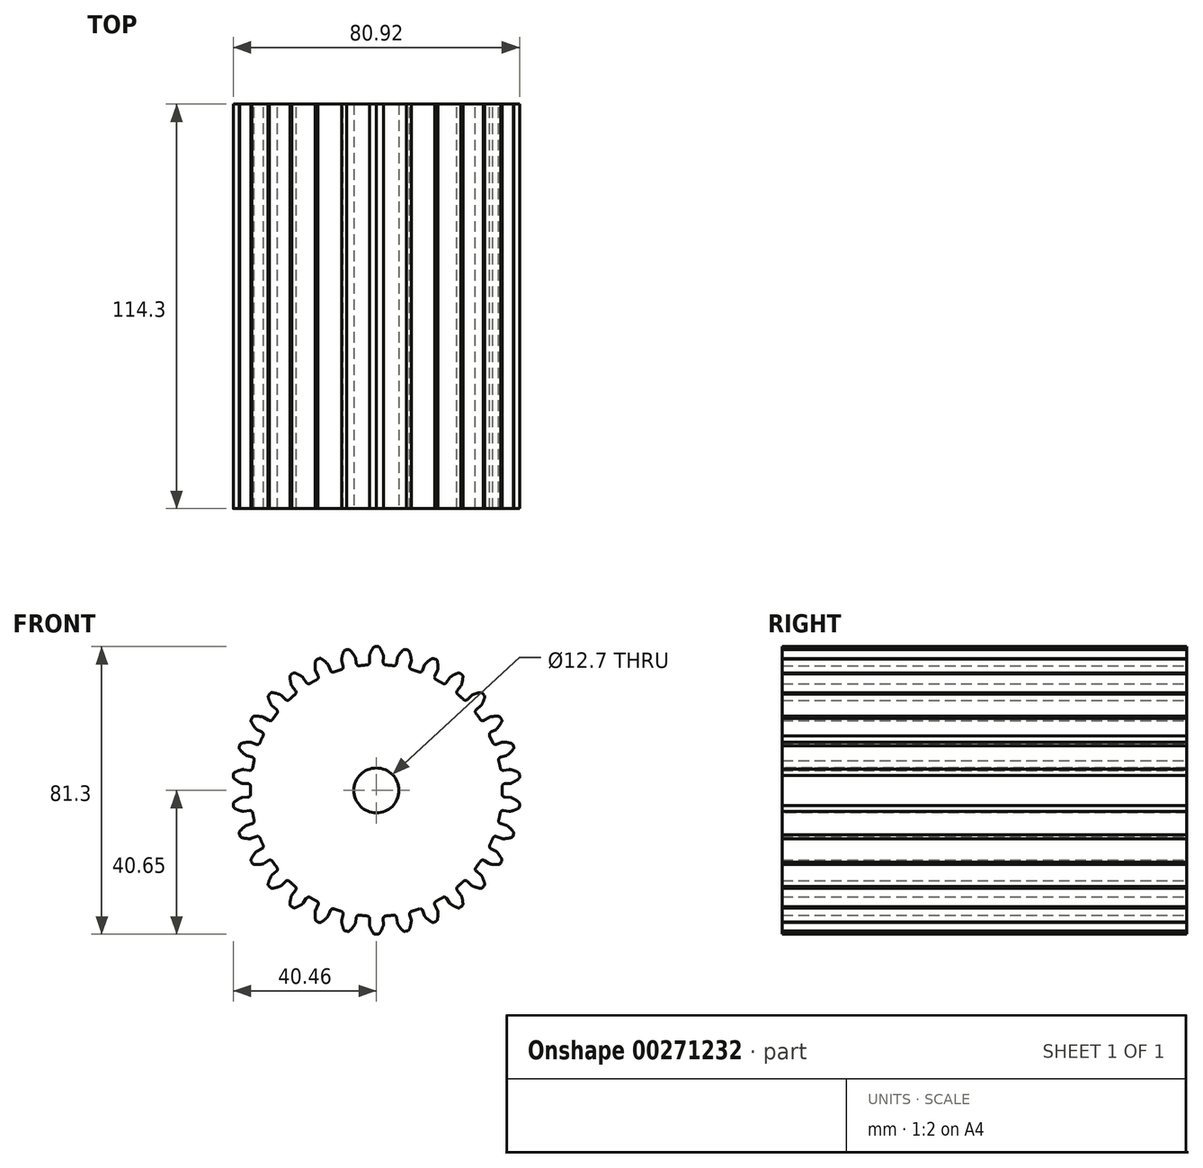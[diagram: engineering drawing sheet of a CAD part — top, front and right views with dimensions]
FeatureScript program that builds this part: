
annotation { "Feature Type Name" : "Feature", "Feature Type Description" : "" }
export const myFeature = defineFeature(function(context is Context, id is Id, definition is map)
    precondition{}
    {
        {
            var Q0;
            Q0=qCreatedBy(makeId("Front.planeOp"),FACE);
            var sketch = newSketch(context, id + "F0", { "sketchPlane" : qUnion([Q0])});
            skArc(sketch, "E0", {"start": v(-2.64, 35.46) * mm, "mid": v(-3.72, 35.37) * mm, "end": v(-4.8, 35.24) * mm});
            skArc(sketch, "E1.trimOffspring", {"start": v(1.94, 38.2) * mm, "mid": v(1.46, 39.34) * mm, "end": v(0.84, 40.41) * mm});
            skLineSegment(sketch, "E2", {"start": v(1.99, 37.9) * mm, "end": v(1.9, 36.3) * mm});
            skLineSegment(sketch, "E3", {"start": v(0.43, 40.64) * mm, "end": v(0, 40.65) * mm});
            skArc(sketch, "E4.MirrorCS", {"start": v(-1.94, 38.2) * mm, "mid": v(-1.5, 39.27) * mm, "end": v(-0.93, 40.28) * mm});
            skLineSegment(sketch, "E5.MirrorCS", {"start": v(-1.99, 37.9) * mm, "end": v(-1.9, 36.3) * mm});
            skLineSegment(sketch, "E6.MirrorCS", {"start": v(-0.28, 40.64) * mm, "end": v(0, 40.65) * mm});
            skPoint(sketch, "E7.visualSharp", {"position": v(-1.86, 35.51) * mm});
            skArc(sketch, "E7.filletArc", {"start": v(-2.64, 35.46) * mm, "mid": v(-2.1, 35.73) * mm, "end": v(-1.9, 36.3) * mm});
            skPoint(sketch, "E8.visualSharp", {"position": v(1.86, 35.51) * mm});
            skArc(sketch, "E8.filletArc", {"start": v(1.9, 36.3) * mm, "mid": v(2.1, 35.73) * mm, "end": v(2.64, 35.46) * mm});
            skPoint(sketch, "E9.visualSharp", {"position": v(2, 38.05) * mm});
            skArc(sketch, "E9.filletArc", {"start": v(1.99, 37.9) * mm, "mid": v(1.98, 38.05) * mm, "end": v(1.94, 38.2) * mm});
            skPoint(sketch, "E10.visualSharp", {"position": v(-2, 38.05) * mm});
            skArc(sketch, "E10.filletArc", {"start": v(-1.94, 38.2) * mm, "mid": v(-1.98, 38.05) * mm, "end": v(-1.99, 37.9) * mm});
            skPoint(sketch, "E11.visualSharp", {"position": v(0.69, 40.63) * mm});
            skArc(sketch, "E11.filletArc", {"start": v(0.84, 40.41) * mm, "mid": v(0.66, 40.58) * mm, "end": v(0.43, 40.64) * mm});
            skPoint(sketch, "E12.visualSharp", {"position": v(-0.69, 40.63) * mm});
            skArc(sketch, "E12.filletArc", {"start": v(-0.28, 40.64) * mm, "mid": v(-0.65, 40.54) * mm, "end": v(-0.93, 40.28) * mm});
            skLineSegment(sketch, "E13.1.0", {"start": v(-9.82, 36.66) * mm, "end": v(-9.4, 35.1) * mm});
            skArc(sketch, "E13.1.1", {"start": v(-9.95, 34.14) * mm, "mid": v(-9.48, 34.51) * mm, "end": v(-9.4, 35.1) * mm});
            skArc(sketch, "E13.1.2", {"start": v(-9.84, 36.96) * mm, "mid": v(-9.63, 38.1) * mm, "end": v(-9.28, 39.2) * mm});
            skArc(sketch, "E13.1.3", {"start": v(-6.04, 37.77) * mm, "mid": v(-6.75, 38.79) * mm, "end": v(-7.58, 39.7) * mm});
            skLineSegment(sketch, "E13.1.4", {"start": v(-5.94, 37.48) * mm, "end": v(-5.69, 35.9) * mm});
            skArc(sketch, "E13.1.5", {"start": v(-5.69, 35.9) * mm, "mid": v(-5.38, 35.38) * mm, "end": v(-4.8, 35.24) * mm});
            skArc(sketch, "E13.1.6", {"start": v(-9.84, 36.96) * mm, "mid": v(-9.85, 36.8) * mm, "end": v(-9.82, 36.66) * mm});
            skArc(sketch, "E13.1.7", {"start": v(-5.94, 37.48) * mm, "mid": v(-5.97, 37.63) * mm, "end": v(-6.04, 37.77) * mm});
            skLineSegment(sketch, "E13.1.8", {"start": v(-8.03, 39.84) * mm, "end": v(-8.45, 39.76) * mm});
            skArc(sketch, "E13.1.9", {"start": v(-7.58, 39.7) * mm, "mid": v(-7.79, 39.83) * mm, "end": v(-8.03, 39.84) * mm});
            skLineSegment(sketch, "E13.1.10", {"start": v(-8.72, 39.7) * mm, "end": v(-8.45, 39.76) * mm});
            skArc(sketch, "E13.1.11", {"start": v(-8.72, 39.7) * mm, "mid": v(-9.06, 39.52) * mm, "end": v(-9.28, 39.2) * mm});
            skLineSegment(sketch, "E13.2.0", {"start": v(-17.23, 33.81) * mm, "end": v(-16.5, 32.38) * mm});
            skArc(sketch, "E13.2.1", {"start": v(-16.83, 31.32) * mm, "mid": v(-16.45, 31.79) * mm, "end": v(-16.5, 32.38) * mm});
            skArc(sketch, "E13.2.2", {"start": v(-17.31, 34.1) * mm, "mid": v(-17.34, 35.26) * mm, "end": v(-17.23, 36.42) * mm});
            skArc(sketch, "E13.2.3", {"start": v(-13.76, 35.69) * mm, "mid": v(-14.66, 36.54) * mm, "end": v(-15.67, 37.26) * mm});
            skLineSegment(sketch, "E13.2.4", {"start": v(-13.6, 35.43) * mm, "end": v(-13.02, 33.93) * mm});
            skArc(sketch, "E13.2.5", {"start": v(-13.02, 33.93) * mm, "mid": v(-12.61, 33.5) * mm, "end": v(-12.02, 33.47) * mm});
            skArc(sketch, "E13.2.6", {"start": v(-17.31, 34.1) * mm, "mid": v(-17.28, 33.95) * mm, "end": v(-17.23, 33.81) * mm});
            skArc(sketch, "E13.2.7", {"start": v(-13.6, 35.43) * mm, "mid": v(-13.67, 35.56) * mm, "end": v(-13.76, 35.69) * mm});
            skLineSegment(sketch, "E13.2.8", {"start": v(-16.14, 37.3) * mm, "end": v(-16.53, 37.13) * mm});
            skArc(sketch, "E13.2.9", {"start": v(-15.67, 37.26) * mm, "mid": v(-15.9, 37.34) * mm, "end": v(-16.14, 37.3) * mm});
            skLineSegment(sketch, "E13.2.10", {"start": v(-16.78, 37.01) * mm, "end": v(-16.53, 37.13) * mm});
            skArc(sketch, "E13.2.11", {"start": v(-16.78, 37.01) * mm, "mid": v(-17.08, 36.77) * mm, "end": v(-17.23, 36.42) * mm});
            skLineSegment(sketch, "E13.3.0", {"start": v(-23.88, 29.5) * mm, "end": v(-22.87, 28.25) * mm});
            skArc(sketch, "E13.3.1", {"start": v(-22.98, 27.14) * mm, "mid": v(-22.7, 27.67) * mm, "end": v(-22.87, 28.25) * mm});
            skArc(sketch, "E13.3.2", {"start": v(-24.02, 29.76) * mm, "mid": v(-24.3, 30.89) * mm, "end": v(-24.43, 32.04) * mm});
            skArc(sketch, "E13.3.3", {"start": v(-20.88, 32.04) * mm, "mid": v(-21.94, 32.69) * mm, "end": v(-23.07, 33.2) * mm});
            skLineSegment(sketch, "E13.3.4", {"start": v(-20.67, 31.83) * mm, "end": v(-19.8, 30.48) * mm});
            skArc(sketch, "E13.3.5", {"start": v(-19.8, 30.48) * mm, "mid": v(-19.3, 30.14) * mm, "end": v(-18.71, 30.24) * mm});
            skArc(sketch, "E13.3.6", {"start": v(-24.02, 29.76) * mm, "mid": v(-23.97, 29.62) * mm, "end": v(-23.88, 29.5) * mm});
            skArc(sketch, "E13.3.7", {"start": v(-20.67, 31.83) * mm, "mid": v(-20.76, 31.95) * mm, "end": v(-20.88, 32.04) * mm});
            skLineSegment(sketch, "E13.3.8", {"start": v(-23.54, 33.13) * mm, "end": v(-23.9, 32.88) * mm});
            skArc(sketch, "E13.3.9", {"start": v(-23.07, 33.2) * mm, "mid": v(-23.31, 33.22) * mm, "end": v(-23.54, 33.13) * mm});
            skLineSegment(sketch, "E13.3.10", {"start": v(-24.11, 32.72) * mm, "end": v(-23.9, 32.88) * mm});
            skArc(sketch, "E13.3.11", {"start": v(-24.11, 32.72) * mm, "mid": v(-24.35, 32.42) * mm, "end": v(-24.43, 32.04) * mm});
            skLineSegment(sketch, "E13.4.0", {"start": v(-29.5, 23.88) * mm, "end": v(-28.25, 22.87) * mm});
            skArc(sketch, "E13.4.1", {"start": v(-28.12, 21.77) * mm, "mid": v(-27.96, 22.35) * mm, "end": v(-28.25, 22.87) * mm});
            skArc(sketch, "E13.4.2", {"start": v(-29.69, 24.11) * mm, "mid": v(-30.19, 25.16) * mm, "end": v(-30.56, 26.26) * mm});
            skArc(sketch, "E13.4.3", {"start": v(-27.09, 27) * mm, "mid": v(-28.26, 27.41) * mm, "end": v(-29.47, 27.67) * mm});
            skLineSegment(sketch, "E13.4.4", {"start": v(-26.83, 26.83) * mm, "end": v(-25.7, 25.7) * mm});
            skArc(sketch, "E13.4.5", {"start": v(-25.7, 25.7) * mm, "mid": v(-25.15, 25.47) * mm, "end": v(-24.59, 25.69) * mm});
            skArc(sketch, "E13.4.6", {"start": v(-29.69, 24.11) * mm, "mid": v(-29.6, 23.99) * mm, "end": v(-29.5, 23.88) * mm});
            skArc(sketch, "E13.4.7", {"start": v(-26.83, 26.83) * mm, "mid": v(-26.95, 26.93) * mm, "end": v(-27.09, 27) * mm});
            skLineSegment(sketch, "E13.4.8", {"start": v(-29.91, 27.51) * mm, "end": v(-30.2, 27.2) * mm});
            skArc(sketch, "E13.4.9", {"start": v(-29.47, 27.67) * mm, "mid": v(-29.71, 27.64) * mm, "end": v(-29.91, 27.51) * mm});
            skLineSegment(sketch, "E13.4.10", {"start": v(-30.39, 26.99) * mm, "end": v(-30.2, 27.2) * mm});
            skArc(sketch, "E13.4.11", {"start": v(-30.39, 26.99) * mm, "mid": v(-30.56, 26.65) * mm, "end": v(-30.56, 26.26) * mm});
            skLineSegment(sketch, "E13.5.0", {"start": v(-33.81, 17.23) * mm, "end": v(-32.38, 16.5) * mm});
            skArc(sketch, "E13.5.1", {"start": v(-32.03, 15.45) * mm, "mid": v(-32, 16.05) * mm, "end": v(-32.38, 16.5) * mm});
            skArc(sketch, "E13.5.2", {"start": v(-34.05, 17.41) * mm, "mid": v(-34.76, 18.34) * mm, "end": v(-35.35, 19.33) * mm});
            skArc(sketch, "E13.5.3", {"start": v(-32.1, 20.78) * mm, "mid": v(-33.34, 20.94) * mm, "end": v(-34.58, 20.94) * mm});
            skLineSegment(sketch, "E13.5.4", {"start": v(-31.83, 20.67) * mm, "end": v(-30.48, 19.8) * mm});
            skArc(sketch, "E13.5.5", {"start": v(-30.48, 19.8) * mm, "mid": v(-29.9, 19.68) * mm, "end": v(-29.4, 20.01) * mm});
            skArc(sketch, "E13.5.6", {"start": v(-34.05, 17.41) * mm, "mid": v(-33.94, 17.31) * mm, "end": v(-33.81, 17.23) * mm});
            skArc(sketch, "E13.5.7", {"start": v(-31.83, 20.67) * mm, "mid": v(-31.96, 20.74) * mm, "end": v(-32.1, 20.78) * mm});
            skLineSegment(sketch, "E13.5.8", {"start": v(-34.98, 20.69) * mm, "end": v(-35.2, 20.32) * mm});
            skArc(sketch, "E13.5.9", {"start": v(-34.58, 20.94) * mm, "mid": v(-34.8, 20.86) * mm, "end": v(-34.98, 20.69) * mm});
            skLineSegment(sketch, "E13.5.10", {"start": v(-35.33, 20.08) * mm, "end": v(-35.2, 20.32) * mm});
            skArc(sketch, "E13.5.11", {"start": v(-35.33, 20.08) * mm, "mid": v(-35.43, 19.7) * mm, "end": v(-35.35, 19.33) * mm});
            skLineSegment(sketch, "E13.6.0", {"start": v(-36.66, 9.82) * mm, "end": v(-35.1, 9.4) * mm});
            skArc(sketch, "E13.6.1", {"start": v(-34.54, 8.45) * mm, "mid": v(-34.63, 9.04) * mm, "end": v(-35.1, 9.4) * mm});
            skArc(sketch, "E13.6.2", {"start": v(-36.93, 9.95) * mm, "mid": v(-37.81, 10.7) * mm, "end": v(-38.6, 11.56) * mm});
            skArc(sketch, "E13.6.3", {"start": v(-35.73, 13.65) * mm, "mid": v(-36.96, 13.55) * mm, "end": v(-38.18, 13.29) * mm});
            skLineSegment(sketch, "E13.6.4", {"start": v(-35.43, 13.6) * mm, "end": v(-33.93, 13.02) * mm});
            skArc(sketch, "E13.6.5", {"start": v(-33.93, 13.02) * mm, "mid": v(-33.33, 13.04) * mm, "end": v(-32.91, 13.47) * mm});
            skArc(sketch, "E13.6.6", {"start": v(-36.93, 9.95) * mm, "mid": v(-36.8, 9.88) * mm, "end": v(-36.66, 9.82) * mm});
            skArc(sketch, "E13.6.7", {"start": v(-35.43, 13.6) * mm, "mid": v(-35.58, 13.64) * mm, "end": v(-35.73, 13.65) * mm});
            skLineSegment(sketch, "E13.6.8", {"start": v(-38.52, 12.97) * mm, "end": v(-38.66, 12.56) * mm});
            skArc(sketch, "E13.6.9", {"start": v(-38.18, 13.29) * mm, "mid": v(-38.39, 13.17) * mm, "end": v(-38.52, 12.97) * mm});
            skLineSegment(sketch, "E13.6.10", {"start": v(-38.74, 12.3) * mm, "end": v(-38.66, 12.56) * mm});
            skArc(sketch, "E13.6.11", {"start": v(-38.74, 12.3) * mm, "mid": v(-38.76, 11.91) * mm, "end": v(-38.6, 11.56) * mm});
            skLineSegment(sketch, "E13.7.0", {"start": v(-37.9, 1.99) * mm, "end": v(-36.3, 1.9) * mm});
            skArc(sketch, "E13.7.1", {"start": v(-35.54, 1.09) * mm, "mid": v(-35.75, 1.65) * mm, "end": v(-36.3, 1.9) * mm});
            skArc(sketch, "E13.7.2", {"start": v(-38.2, 2.06) * mm, "mid": v(-39.21, 2.61) * mm, "end": v(-40.16, 3.29) * mm});
            skArc(sketch, "E13.7.3", {"start": v(-37.78, 5.93) * mm, "mid": v(-38.97, 5.57) * mm, "end": v(-40.1, 5.06) * mm});
            skLineSegment(sketch, "E13.7.4", {"start": v(-37.48, 5.94) * mm, "end": v(-35.9, 5.69) * mm});
            skArc(sketch, "E13.7.5", {"start": v(-35.9, 5.69) * mm, "mid": v(-35.31, 5.82) * mm, "end": v(-35, 6.33) * mm});
            skArc(sketch, "E13.7.6", {"start": v(-38.2, 2.06) * mm, "mid": v(-38.05, 2) * mm, "end": v(-37.9, 1.99) * mm});
            skArc(sketch, "E13.7.7", {"start": v(-37.48, 5.94) * mm, "mid": v(-37.63, 5.95) * mm, "end": v(-37.78, 5.93) * mm});
            skLineSegment(sketch, "E13.7.8", {"start": v(-40.37, 4.67) * mm, "end": v(-40.42, 4.25) * mm});
            skArc(sketch, "E13.7.9", {"start": v(-40.1, 5.06) * mm, "mid": v(-40.29, 4.9) * mm, "end": v(-40.37, 4.67) * mm});
            skLineSegment(sketch, "E13.7.10", {"start": v(-40.45, 3.97) * mm, "end": v(-40.42, 4.25) * mm});
            skArc(sketch, "E13.7.11", {"start": v(-40.45, 3.97) * mm, "mid": v(-40.39, 3.6) * mm, "end": v(-40.16, 3.29) * mm});
            skLineSegment(sketch, "E13.8.0", {"start": v(-37.48, -5.94) * mm, "end": v(-35.9, -5.69) * mm});
            skArc(sketch, "E13.8.1", {"start": v(-35, -6.33) * mm, "mid": v(-35.31, -5.82) * mm, "end": v(-35.9, -5.69) * mm});
            skArc(sketch, "E13.8.2", {"start": v(-37.78, -5.93) * mm, "mid": v(-38.9, -5.6) * mm, "end": v(-39.96, -5.14) * mm});
            skArc(sketch, "E13.8.3", {"start": v(-38.2, -2.06) * mm, "mid": v(-39.28, -2.66) * mm, "end": v(-40.28, -3.39) * mm});
            skLineSegment(sketch, "E13.8.4", {"start": v(-37.9, -1.99) * mm, "end": v(-36.3, -1.9) * mm});
            skArc(sketch, "E13.8.5", {"start": v(-36.3, -1.9) * mm, "mid": v(-35.75, -1.65) * mm, "end": v(-35.54, -1.09) * mm});
            skArc(sketch, "E13.8.6", {"start": v(-37.78, -5.93) * mm, "mid": v(-37.63, -5.95) * mm, "end": v(-37.48, -5.94) * mm});
            skArc(sketch, "E13.8.7", {"start": v(-37.9, -1.99) * mm, "mid": v(-38.05, -2) * mm, "end": v(-38.2, -2.06) * mm});
            skLineSegment(sketch, "E13.8.8", {"start": v(-40.46, -3.82) * mm, "end": v(-40.42, -4.25) * mm});
            skArc(sketch, "E13.8.9", {"start": v(-40.28, -3.39) * mm, "mid": v(-40.42, -3.58) * mm, "end": v(-40.46, -3.82) * mm});
            skLineSegment(sketch, "E13.8.10", {"start": v(-40.39, -4.52) * mm, "end": v(-40.42, -4.25) * mm});
            skArc(sketch, "E13.8.11", {"start": v(-40.39, -4.52) * mm, "mid": v(-40.25, -4.88) * mm, "end": v(-39.96, -5.14) * mm});
            skLineSegment(sketch, "E13.9.0", {"start": v(-35.43, -13.6) * mm, "end": v(-33.93, -13.02) * mm});
            skArc(sketch, "E13.9.1", {"start": v(-32.91, -13.47) * mm, "mid": v(-33.33, -13.04) * mm, "end": v(-33.93, -13.02) * mm});
            skArc(sketch, "E13.9.2", {"start": v(-35.73, -13.65) * mm, "mid": v(-36.88, -13.56) * mm, "end": v(-38.02, -13.33) * mm});
            skArc(sketch, "E13.9.3", {"start": v(-36.93, -9.95) * mm, "mid": v(-37.87, -10.76) * mm, "end": v(-38.7, -11.69) * mm});
            skLineSegment(sketch, "E13.9.4", {"start": v(-36.66, -9.82) * mm, "end": v(-35.1, -9.4) * mm});
            skArc(sketch, "E13.9.5", {"start": v(-35.1, -9.4) * mm, "mid": v(-34.63, -9.04) * mm, "end": v(-34.54, -8.45) * mm});
            skArc(sketch, "E13.9.6", {"start": v(-35.73, -13.65) * mm, "mid": v(-35.58, -13.64) * mm, "end": v(-35.43, -13.6) * mm});
            skArc(sketch, "E13.9.7", {"start": v(-36.66, -9.82) * mm, "mid": v(-36.8, -9.88) * mm, "end": v(-36.93, -9.95) * mm});
            skLineSegment(sketch, "E13.9.8", {"start": v(-38.78, -12.15) * mm, "end": v(-38.66, -12.56) * mm});
            skArc(sketch, "E13.9.9", {"start": v(-38.7, -11.69) * mm, "mid": v(-38.8, -11.9) * mm, "end": v(-38.78, -12.15) * mm});
            skLineSegment(sketch, "E13.9.10", {"start": v(-38.57, -12.82) * mm, "end": v(-38.66, -12.56) * mm});
            skArc(sketch, "E13.9.11", {"start": v(-38.57, -12.82) * mm, "mid": v(-38.36, -13.15) * mm, "end": v(-38.02, -13.33) * mm});
            skLineSegment(sketch, "E13.10.0", {"start": v(-31.83, -20.67) * mm, "end": v(-30.48, -19.8) * mm});
            skArc(sketch, "E13.10.1", {"start": v(-29.4, -20.01) * mm, "mid": v(-29.9, -19.68) * mm, "end": v(-30.48, -19.8) * mm});
            skArc(sketch, "E13.10.2", {"start": v(-32.1, -20.78) * mm, "mid": v(-33.26, -20.93) * mm, "end": v(-34.42, -20.95) * mm});
            skArc(sketch, "E13.10.3", {"start": v(-34.05, -17.41) * mm, "mid": v(-34.8, -18.4) * mm, "end": v(-35.42, -19.48) * mm});
            skLineSegment(sketch, "E13.10.4", {"start": v(-33.81, -17.23) * mm, "end": v(-32.38, -16.5) * mm});
            skArc(sketch, "E13.10.5", {"start": v(-32.38, -16.5) * mm, "mid": v(-32, -16.05) * mm, "end": v(-32.03, -15.45) * mm});
            skArc(sketch, "E13.10.6", {"start": v(-32.1, -20.78) * mm, "mid": v(-31.96, -20.74) * mm, "end": v(-31.83, -20.67) * mm});
            skArc(sketch, "E13.10.7", {"start": v(-33.81, -17.23) * mm, "mid": v(-33.94, -17.31) * mm, "end": v(-34.05, -17.41) * mm});
            skLineSegment(sketch, "E13.10.8", {"start": v(-35.4, -19.95) * mm, "end": v(-35.2, -20.32) * mm});
            skArc(sketch, "E13.10.9", {"start": v(-35.42, -19.48) * mm, "mid": v(-35.47, -19.72) * mm, "end": v(-35.4, -19.95) * mm});
            skLineSegment(sketch, "E13.10.10", {"start": v(-35.06, -20.56) * mm, "end": v(-35.2, -20.32) * mm});
            skArc(sketch, "E13.10.11", {"start": v(-35.06, -20.56) * mm, "mid": v(-34.79, -20.83) * mm, "end": v(-34.42, -20.95) * mm});
            skLineSegment(sketch, "E13.11.0", {"start": v(-26.83, -26.83) * mm, "end": v(-25.7, -25.7) * mm});
            skArc(sketch, "E13.11.1", {"start": v(-24.59, -25.69) * mm, "mid": v(-25.15, -25.47) * mm, "end": v(-25.7, -25.7) * mm});
            skArc(sketch, "E13.11.2", {"start": v(-27.09, -27) * mm, "mid": v(-28.18, -27.4) * mm, "end": v(-29.31, -27.64) * mm});
            skArc(sketch, "E13.11.3", {"start": v(-29.69, -24.11) * mm, "mid": v(-30.22, -25.24) * mm, "end": v(-30.6, -26.42) * mm});
            skLineSegment(sketch, "E13.11.4", {"start": v(-29.5, -23.88) * mm, "end": v(-28.25, -22.87) * mm});
            skArc(sketch, "E13.11.5", {"start": v(-28.25, -22.87) * mm, "mid": v(-27.96, -22.35) * mm, "end": v(-28.12, -21.77) * mm});
            skArc(sketch, "E13.11.6", {"start": v(-27.09, -27) * mm, "mid": v(-26.95, -26.93) * mm, "end": v(-26.83, -26.83) * mm});
            skArc(sketch, "E13.11.7", {"start": v(-29.5, -23.88) * mm, "mid": v(-29.6, -23.99) * mm, "end": v(-29.69, -24.11) * mm});
            skLineSegment(sketch, "E13.11.8", {"start": v(-30.49, -26.87) * mm, "end": v(-30.2, -27.2) * mm});
            skArc(sketch, "E13.11.9", {"start": v(-30.6, -26.42) * mm, "mid": v(-30.6, -26.66) * mm, "end": v(-30.49, -26.87) * mm});
            skLineSegment(sketch, "E13.11.10", {"start": v(-30.02, -27.4) * mm, "end": v(-30.2, -27.2) * mm});
            skArc(sketch, "E13.11.11", {"start": v(-30.02, -27.4) * mm, "mid": v(-29.7, -27.6) * mm, "end": v(-29.31, -27.64) * mm});
            skLineSegment(sketch, "E13.12.0", {"start": v(-20.67, -31.83) * mm, "end": v(-19.8, -30.48) * mm});
            skArc(sketch, "E13.12.1", {"start": v(-18.71, -30.24) * mm, "mid": v(-19.3, -30.14) * mm, "end": v(-19.8, -30.48) * mm});
            skArc(sketch, "E13.12.2", {"start": v(-20.88, -32.04) * mm, "mid": v(-21.87, -32.65) * mm, "end": v(-22.92, -33.13) * mm});
            skArc(sketch, "E13.12.3", {"start": v(-24.02, -29.76) * mm, "mid": v(-24.3, -30.97) * mm, "end": v(-24.44, -32.2) * mm});
            skLineSegment(sketch, "E13.12.4", {"start": v(-23.88, -29.5) * mm, "end": v(-22.87, -28.25) * mm});
            skArc(sketch, "E13.12.5", {"start": v(-22.87, -28.25) * mm, "mid": v(-22.7, -27.67) * mm, "end": v(-22.98, -27.14) * mm});
            skArc(sketch, "E13.12.6", {"start": v(-20.88, -32.04) * mm, "mid": v(-20.76, -31.95) * mm, "end": v(-20.67, -31.83) * mm});
            skArc(sketch, "E13.12.7", {"start": v(-23.88, -29.5) * mm, "mid": v(-23.97, -29.62) * mm, "end": v(-24.02, -29.76) * mm});
            skLineSegment(sketch, "E13.12.8", {"start": v(-24.23, -32.63) * mm, "end": v(-23.9, -32.88) * mm});
            skArc(sketch, "E13.12.9", {"start": v(-24.44, -32.2) * mm, "mid": v(-24.39, -32.44) * mm, "end": v(-24.23, -32.63) * mm});
            skLineSegment(sketch, "E13.12.10", {"start": v(-23.66, -33.04) * mm, "end": v(-23.9, -32.88) * mm});
            skArc(sketch, "E13.12.11", {"start": v(-23.66, -33.04) * mm, "mid": v(-23.3, -33.18) * mm, "end": v(-22.92, -33.13) * mm});
            skLineSegment(sketch, "E13.13.0", {"start": v(-13.6, -35.43) * mm, "end": v(-13.02, -33.93) * mm});
            skArc(sketch, "E13.13.1", {"start": v(-12.02, -33.47) * mm, "mid": v(-12.61, -33.5) * mm, "end": v(-13.02, -33.93) * mm});
            skArc(sketch, "E13.13.2", {"start": v(-13.76, -35.69) * mm, "mid": v(-14.6, -36.48) * mm, "end": v(-15.53, -37.18) * mm});
            skArc(sketch, "E13.13.3", {"start": v(-17.31, -34.1) * mm, "mid": v(-17.34, -35.34) * mm, "end": v(-17.2, -36.58) * mm});
            skLineSegment(sketch, "E13.13.4", {"start": v(-17.23, -33.81) * mm, "end": v(-16.5, -32.38) * mm});
            skArc(sketch, "E13.13.5", {"start": v(-16.5, -32.38) * mm, "mid": v(-16.45, -31.79) * mm, "end": v(-16.83, -31.32) * mm});
            skArc(sketch, "E13.13.6", {"start": v(-13.76, -35.69) * mm, "mid": v(-13.67, -35.56) * mm, "end": v(-13.6, -35.43) * mm});
            skArc(sketch, "E13.13.7", {"start": v(-17.23, -33.81) * mm, "mid": v(-17.28, -33.95) * mm, "end": v(-17.31, -34.1) * mm});
            skLineSegment(sketch, "E13.13.8", {"start": v(-16.92, -36.95) * mm, "end": v(-16.53, -37.13) * mm});
            skArc(sketch, "E13.13.9", {"start": v(-17.2, -36.58) * mm, "mid": v(-17.1, -36.8) * mm, "end": v(-16.92, -36.95) * mm});
            skLineSegment(sketch, "E13.13.10", {"start": v(-16.28, -37.24) * mm, "end": v(-16.53, -37.13) * mm});
            skArc(sketch, "E13.13.11", {"start": v(-16.28, -37.24) * mm, "mid": v(-15.9, -37.3) * mm, "end": v(-15.53, -37.18) * mm});
            skLineSegment(sketch, "E13.14.0", {"start": v(-5.94, -37.48) * mm, "end": v(-5.69, -35.9) * mm});
            skArc(sketch, "E13.14.1", {"start": v(-4.8, -35.24) * mm, "mid": v(-5.38, -35.38) * mm, "end": v(-5.69, -35.9) * mm});
            skArc(sketch, "E13.14.2", {"start": v(-6.04, -37.77) * mm, "mid": v(-6.7, -38.72) * mm, "end": v(-7.46, -39.6) * mm});
            skArc(sketch, "E13.14.3", {"start": v(-9.84, -36.96) * mm, "mid": v(-9.61, -38.18) * mm, "end": v(-9.23, -39.36) * mm});
            skLineSegment(sketch, "E13.14.4", {"start": v(-9.82, -36.66) * mm, "end": v(-9.4, -35.1) * mm});
            skArc(sketch, "E13.14.5", {"start": v(-9.4, -35.1) * mm, "mid": v(-9.48, -34.51) * mm, "end": v(-9.95, -34.14) * mm});
            skArc(sketch, "E13.14.6", {"start": v(-6.04, -37.77) * mm, "mid": v(-5.97, -37.63) * mm, "end": v(-5.94, -37.48) * mm});
            skArc(sketch, "E13.14.7", {"start": v(-9.82, -36.66) * mm, "mid": v(-9.85, -36.8) * mm, "end": v(-9.84, -36.96) * mm});
            skLineSegment(sketch, "E13.14.8", {"start": v(-8.87, -39.66) * mm, "end": v(-8.45, -39.76) * mm});
            skArc(sketch, "E13.14.9", {"start": v(-9.23, -39.36) * mm, "mid": v(-9.08, -39.55) * mm, "end": v(-8.87, -39.66) * mm});
            skLineSegment(sketch, "E13.14.10", {"start": v(-8.18, -39.81) * mm, "end": v(-8.45, -39.76) * mm});
            skArc(sketch, "E13.14.11", {"start": v(-8.18, -39.81) * mm, "mid": v(-7.8, -39.8) * mm, "end": v(-7.46, -39.6) * mm});
            skLineSegment(sketch, "E13.15.0", {"start": v(1.99, -37.9) * mm, "end": v(1.9, -36.3) * mm});
            skArc(sketch, "E13.15.1", {"start": v(2.64, -35.46) * mm, "mid": v(2.1, -35.73) * mm, "end": v(1.9, -36.3) * mm});
            skArc(sketch, "E13.15.2", {"start": v(1.94, -38.2) * mm, "mid": v(1.5, -39.27) * mm, "end": v(0.93, -40.28) * mm});
            skArc(sketch, "E13.15.3", {"start": v(-1.94, -38.2) * mm, "mid": v(-1.46, -39.34) * mm, "end": v(-0.84, -40.41) * mm});
            skLineSegment(sketch, "E13.15.4", {"start": v(-1.99, -37.9) * mm, "end": v(-1.9, -36.3) * mm});
            skArc(sketch, "E13.15.5", {"start": v(-1.9, -36.3) * mm, "mid": v(-2.1, -35.73) * mm, "end": v(-2.64, -35.46) * mm});
            skArc(sketch, "E13.15.6", {"start": v(1.94, -38.2) * mm, "mid": v(1.98, -38.05) * mm, "end": v(1.99, -37.9) * mm});
            skArc(sketch, "E13.15.7", {"start": v(-1.99, -37.9) * mm, "mid": v(-1.98, -38.05) * mm, "end": v(-1.94, -38.2) * mm});
            skLineSegment(sketch, "E13.15.8", {"start": v(-0.43, -40.64) * mm, "end": v(0, -40.65) * mm});
            skArc(sketch, "E13.15.9", {"start": v(-0.84, -40.41) * mm, "mid": v(-0.66, -40.58) * mm, "end": v(-0.43, -40.64) * mm});
            skLineSegment(sketch, "E13.15.10", {"start": v(0.28, -40.64) * mm, "end": v(0, -40.65) * mm});
            skArc(sketch, "E13.15.11", {"start": v(0.28, -40.64) * mm, "mid": v(0.65, -40.54) * mm, "end": v(0.93, -40.28) * mm});
            skLineSegment(sketch, "E13.16.0", {"start": v(9.82, -36.66) * mm, "end": v(9.4, -35.1) * mm});
            skArc(sketch, "E13.16.1", {"start": v(9.95, -34.14) * mm, "mid": v(9.48, -34.51) * mm, "end": v(9.4, -35.1) * mm});
            skArc(sketch, "E13.16.2", {"start": v(9.84, -36.96) * mm, "mid": v(9.63, -38.1) * mm, "end": v(9.28, -39.2) * mm});
            skArc(sketch, "E13.16.3", {"start": v(6.04, -37.77) * mm, "mid": v(6.75, -38.79) * mm, "end": v(7.58, -39.7) * mm});
            skLineSegment(sketch, "E13.16.4", {"start": v(5.94, -37.48) * mm, "end": v(5.69, -35.9) * mm});
            skArc(sketch, "E13.16.5", {"start": v(5.69, -35.9) * mm, "mid": v(5.38, -35.38) * mm, "end": v(4.8, -35.24) * mm});
            skArc(sketch, "E13.16.6", {"start": v(9.84, -36.96) * mm, "mid": v(9.85, -36.8) * mm, "end": v(9.82, -36.66) * mm});
            skArc(sketch, "E13.16.7", {"start": v(5.94, -37.48) * mm, "mid": v(5.97, -37.63) * mm, "end": v(6.04, -37.77) * mm});
            skLineSegment(sketch, "E13.16.8", {"start": v(8.03, -39.84) * mm, "end": v(8.45, -39.76) * mm});
            skArc(sketch, "E13.16.9", {"start": v(7.58, -39.7) * mm, "mid": v(7.79, -39.83) * mm, "end": v(8.03, -39.84) * mm});
            skLineSegment(sketch, "E13.16.10", {"start": v(8.72, -39.7) * mm, "end": v(8.45, -39.76) * mm});
            skArc(sketch, "E13.16.11", {"start": v(8.72, -39.7) * mm, "mid": v(9.06, -39.52) * mm, "end": v(9.28, -39.2) * mm});
            skLineSegment(sketch, "E13.17.0", {"start": v(17.23, -33.81) * mm, "end": v(16.5, -32.38) * mm});
            skArc(sketch, "E13.17.1", {"start": v(16.83, -31.32) * mm, "mid": v(16.45, -31.79) * mm, "end": v(16.5, -32.38) * mm});
            skArc(sketch, "E13.17.2", {"start": v(17.31, -34.1) * mm, "mid": v(17.34, -35.26) * mm, "end": v(17.23, -36.42) * mm});
            skArc(sketch, "E13.17.3", {"start": v(13.76, -35.69) * mm, "mid": v(14.66, -36.54) * mm, "end": v(15.67, -37.26) * mm});
            skLineSegment(sketch, "E13.17.4", {"start": v(13.6, -35.43) * mm, "end": v(13.02, -33.93) * mm});
            skArc(sketch, "E13.17.5", {"start": v(13.02, -33.93) * mm, "mid": v(12.61, -33.5) * mm, "end": v(12.02, -33.47) * mm});
            skArc(sketch, "E13.17.6", {"start": v(17.31, -34.1) * mm, "mid": v(17.28, -33.95) * mm, "end": v(17.23, -33.81) * mm});
            skArc(sketch, "E13.17.7", {"start": v(13.6, -35.43) * mm, "mid": v(13.67, -35.56) * mm, "end": v(13.76, -35.69) * mm});
            skLineSegment(sketch, "E13.17.8", {"start": v(16.14, -37.3) * mm, "end": v(16.53, -37.13) * mm});
            skArc(sketch, "E13.17.9", {"start": v(15.67, -37.26) * mm, "mid": v(15.9, -37.34) * mm, "end": v(16.14, -37.3) * mm});
            skLineSegment(sketch, "E13.17.10", {"start": v(16.78, -37.01) * mm, "end": v(16.53, -37.13) * mm});
            skArc(sketch, "E13.17.11", {"start": v(16.78, -37.01) * mm, "mid": v(17.08, -36.77) * mm, "end": v(17.23, -36.42) * mm});
            skLineSegment(sketch, "E13.18.0", {"start": v(23.88, -29.5) * mm, "end": v(22.87, -28.25) * mm});
            skArc(sketch, "E13.18.1", {"start": v(22.98, -27.14) * mm, "mid": v(22.7, -27.67) * mm, "end": v(22.87, -28.25) * mm});
            skArc(sketch, "E13.18.2", {"start": v(24.02, -29.76) * mm, "mid": v(24.3, -30.89) * mm, "end": v(24.43, -32.04) * mm});
            skArc(sketch, "E13.18.3", {"start": v(20.88, -32.04) * mm, "mid": v(21.94, -32.69) * mm, "end": v(23.07, -33.2) * mm});
            skLineSegment(sketch, "E13.18.4", {"start": v(20.67, -31.83) * mm, "end": v(19.8, -30.48) * mm});
            skArc(sketch, "E13.18.5", {"start": v(19.8, -30.48) * mm, "mid": v(19.3, -30.14) * mm, "end": v(18.71, -30.24) * mm});
            skArc(sketch, "E13.18.6", {"start": v(24.02, -29.76) * mm, "mid": v(23.97, -29.62) * mm, "end": v(23.88, -29.5) * mm});
            skArc(sketch, "E13.18.7", {"start": v(20.67, -31.83) * mm, "mid": v(20.76, -31.95) * mm, "end": v(20.88, -32.04) * mm});
            skLineSegment(sketch, "E13.18.8", {"start": v(23.54, -33.13) * mm, "end": v(23.9, -32.88) * mm});
            skArc(sketch, "E13.18.9", {"start": v(23.07, -33.2) * mm, "mid": v(23.31, -33.22) * mm, "end": v(23.54, -33.13) * mm});
            skLineSegment(sketch, "E13.18.10", {"start": v(24.11, -32.72) * mm, "end": v(23.9, -32.88) * mm});
            skArc(sketch, "E13.18.11", {"start": v(24.11, -32.72) * mm, "mid": v(24.35, -32.42) * mm, "end": v(24.43, -32.04) * mm});
            skLineSegment(sketch, "E13.19.0", {"start": v(29.5, -23.88) * mm, "end": v(28.25, -22.87) * mm});
            skArc(sketch, "E13.19.1", {"start": v(28.12, -21.77) * mm, "mid": v(27.96, -22.35) * mm, "end": v(28.25, -22.87) * mm});
            skArc(sketch, "E13.19.2", {"start": v(29.69, -24.11) * mm, "mid": v(30.19, -25.16) * mm, "end": v(30.56, -26.26) * mm});
            skArc(sketch, "E13.19.3", {"start": v(27.09, -27) * mm, "mid": v(28.26, -27.41) * mm, "end": v(29.47, -27.67) * mm});
            skLineSegment(sketch, "E13.19.4", {"start": v(26.83, -26.83) * mm, "end": v(25.7, -25.7) * mm});
            skArc(sketch, "E13.19.5", {"start": v(25.7, -25.7) * mm, "mid": v(25.15, -25.47) * mm, "end": v(24.59, -25.69) * mm});
            skArc(sketch, "E13.19.6", {"start": v(29.69, -24.11) * mm, "mid": v(29.6, -23.99) * mm, "end": v(29.5, -23.88) * mm});
            skArc(sketch, "E13.19.7", {"start": v(26.83, -26.83) * mm, "mid": v(26.95, -26.93) * mm, "end": v(27.09, -27) * mm});
            skLineSegment(sketch, "E13.19.8", {"start": v(29.91, -27.51) * mm, "end": v(30.2, -27.2) * mm});
            skArc(sketch, "E13.19.9", {"start": v(29.47, -27.67) * mm, "mid": v(29.71, -27.64) * mm, "end": v(29.91, -27.51) * mm});
            skLineSegment(sketch, "E13.19.10", {"start": v(30.39, -26.99) * mm, "end": v(30.2, -27.2) * mm});
            skArc(sketch, "E13.19.11", {"start": v(30.39, -26.99) * mm, "mid": v(30.56, -26.65) * mm, "end": v(30.56, -26.26) * mm});
            skLineSegment(sketch, "E13.20.0", {"start": v(33.81, -17.23) * mm, "end": v(32.38, -16.5) * mm});
            skArc(sketch, "E13.20.1", {"start": v(32.03, -15.45) * mm, "mid": v(32, -16.05) * mm, "end": v(32.38, -16.5) * mm});
            skArc(sketch, "E13.20.2", {"start": v(34.05, -17.41) * mm, "mid": v(34.76, -18.34) * mm, "end": v(35.35, -19.33) * mm});
            skArc(sketch, "E13.20.3", {"start": v(32.1, -20.78) * mm, "mid": v(33.34, -20.94) * mm, "end": v(34.58, -20.94) * mm});
            skLineSegment(sketch, "E13.20.4", {"start": v(31.83, -20.67) * mm, "end": v(30.48, -19.8) * mm});
            skArc(sketch, "E13.20.5", {"start": v(30.48, -19.8) * mm, "mid": v(29.9, -19.68) * mm, "end": v(29.4, -20.01) * mm});
            skArc(sketch, "E13.20.6", {"start": v(34.05, -17.41) * mm, "mid": v(33.94, -17.31) * mm, "end": v(33.81, -17.23) * mm});
            skArc(sketch, "E13.20.7", {"start": v(31.83, -20.67) * mm, "mid": v(31.96, -20.74) * mm, "end": v(32.1, -20.78) * mm});
            skLineSegment(sketch, "E13.20.8", {"start": v(34.98, -20.69) * mm, "end": v(35.2, -20.32) * mm});
            skArc(sketch, "E13.20.9", {"start": v(34.58, -20.94) * mm, "mid": v(34.8, -20.86) * mm, "end": v(34.98, -20.69) * mm});
            skLineSegment(sketch, "E13.20.10", {"start": v(35.33, -20.08) * mm, "end": v(35.2, -20.32) * mm});
            skArc(sketch, "E13.20.11", {"start": v(35.33, -20.08) * mm, "mid": v(35.43, -19.7) * mm, "end": v(35.35, -19.33) * mm});
            skLineSegment(sketch, "E13.21.0", {"start": v(36.66, -9.82) * mm, "end": v(35.1, -9.4) * mm});
            skArc(sketch, "E13.21.1", {"start": v(34.54, -8.45) * mm, "mid": v(34.63, -9.04) * mm, "end": v(35.1, -9.4) * mm});
            skArc(sketch, "E13.21.2", {"start": v(36.93, -9.95) * mm, "mid": v(37.81, -10.7) * mm, "end": v(38.6, -11.56) * mm});
            skArc(sketch, "E13.21.3", {"start": v(35.73, -13.65) * mm, "mid": v(36.96, -13.55) * mm, "end": v(38.18, -13.29) * mm});
            skLineSegment(sketch, "E13.21.4", {"start": v(35.43, -13.6) * mm, "end": v(33.93, -13.02) * mm});
            skArc(sketch, "E13.21.5", {"start": v(33.93, -13.02) * mm, "mid": v(33.33, -13.04) * mm, "end": v(32.91, -13.47) * mm});
            skArc(sketch, "E13.21.6", {"start": v(36.93, -9.95) * mm, "mid": v(36.8, -9.88) * mm, "end": v(36.66, -9.82) * mm});
            skArc(sketch, "E13.21.7", {"start": v(35.43, -13.6) * mm, "mid": v(35.58, -13.64) * mm, "end": v(35.73, -13.65) * mm});
            skLineSegment(sketch, "E13.21.8", {"start": v(38.52, -12.97) * mm, "end": v(38.66, -12.56) * mm});
            skArc(sketch, "E13.21.9", {"start": v(38.18, -13.29) * mm, "mid": v(38.39, -13.17) * mm, "end": v(38.52, -12.97) * mm});
            skLineSegment(sketch, "E13.21.10", {"start": v(38.74, -12.3) * mm, "end": v(38.66, -12.56) * mm});
            skArc(sketch, "E13.21.11", {"start": v(38.74, -12.3) * mm, "mid": v(38.76, -11.91) * mm, "end": v(38.6, -11.56) * mm});
            skLineSegment(sketch, "E13.22.0", {"start": v(37.9, -1.99) * mm, "end": v(36.3, -1.9) * mm});
            skArc(sketch, "E13.22.1", {"start": v(35.54, -1.09) * mm, "mid": v(35.75, -1.65) * mm, "end": v(36.3, -1.9) * mm});
            skArc(sketch, "E13.22.2", {"start": v(38.2, -2.06) * mm, "mid": v(39.21, -2.61) * mm, "end": v(40.16, -3.29) * mm});
            skArc(sketch, "E13.22.3", {"start": v(37.78, -5.93) * mm, "mid": v(38.97, -5.57) * mm, "end": v(40.1, -5.06) * mm});
            skLineSegment(sketch, "E13.22.4", {"start": v(37.48, -5.94) * mm, "end": v(35.9, -5.69) * mm});
            skArc(sketch, "E13.22.5", {"start": v(35.9, -5.69) * mm, "mid": v(35.31, -5.82) * mm, "end": v(35, -6.33) * mm});
            skArc(sketch, "E13.22.6", {"start": v(38.2, -2.06) * mm, "mid": v(38.05, -2) * mm, "end": v(37.9, -1.99) * mm});
            skArc(sketch, "E13.22.7", {"start": v(37.48, -5.94) * mm, "mid": v(37.63, -5.95) * mm, "end": v(37.78, -5.93) * mm});
            skLineSegment(sketch, "E13.22.8", {"start": v(40.37, -4.67) * mm, "end": v(40.42, -4.25) * mm});
            skArc(sketch, "E13.22.9", {"start": v(40.1, -5.06) * mm, "mid": v(40.29, -4.9) * mm, "end": v(40.37, -4.67) * mm});
            skLineSegment(sketch, "E13.22.10", {"start": v(40.45, -3.97) * mm, "end": v(40.42, -4.25) * mm});
            skArc(sketch, "E13.22.11", {"start": v(40.45, -3.97) * mm, "mid": v(40.39, -3.6) * mm, "end": v(40.16, -3.29) * mm});
            skLineSegment(sketch, "E13.23.0", {"start": v(37.48, 5.94) * mm, "end": v(35.9, 5.69) * mm});
            skArc(sketch, "E13.23.1", {"start": v(35, 6.33) * mm, "mid": v(35.31, 5.82) * mm, "end": v(35.9, 5.69) * mm});
            skArc(sketch, "E13.23.2", {"start": v(37.78, 5.93) * mm, "mid": v(38.9, 5.6) * mm, "end": v(39.96, 5.14) * mm});
            skArc(sketch, "E13.23.3", {"start": v(38.2, 2.06) * mm, "mid": v(39.28, 2.66) * mm, "end": v(40.28, 3.39) * mm});
            skLineSegment(sketch, "E13.23.4", {"start": v(37.9, 1.99) * mm, "end": v(36.3, 1.9) * mm});
            skArc(sketch, "E13.23.5", {"start": v(36.3, 1.9) * mm, "mid": v(35.75, 1.65) * mm, "end": v(35.54, 1.09) * mm});
            skArc(sketch, "E13.23.6", {"start": v(37.78, 5.93) * mm, "mid": v(37.63, 5.95) * mm, "end": v(37.48, 5.94) * mm});
            skArc(sketch, "E13.23.7", {"start": v(37.9, 1.99) * mm, "mid": v(38.05, 2) * mm, "end": v(38.2, 2.06) * mm});
            skLineSegment(sketch, "E13.23.8", {"start": v(40.46, 3.82) * mm, "end": v(40.42, 4.25) * mm});
            skArc(sketch, "E13.23.9", {"start": v(40.28, 3.39) * mm, "mid": v(40.42, 3.58) * mm, "end": v(40.46, 3.82) * mm});
            skLineSegment(sketch, "E13.23.10", {"start": v(40.39, 4.52) * mm, "end": v(40.42, 4.25) * mm});
            skArc(sketch, "E13.23.11", {"start": v(40.39, 4.52) * mm, "mid": v(40.25, 4.88) * mm, "end": v(39.96, 5.14) * mm});
            skLineSegment(sketch, "E13.24.0", {"start": v(35.43, 13.6) * mm, "end": v(33.93, 13.02) * mm});
            skArc(sketch, "E13.24.1", {"start": v(32.91, 13.47) * mm, "mid": v(33.33, 13.04) * mm, "end": v(33.93, 13.02) * mm});
            skArc(sketch, "E13.24.2", {"start": v(35.73, 13.65) * mm, "mid": v(36.88, 13.56) * mm, "end": v(38.02, 13.33) * mm});
            skArc(sketch, "E13.24.3", {"start": v(36.93, 9.95) * mm, "mid": v(37.87, 10.76) * mm, "end": v(38.7, 11.69) * mm});
            skLineSegment(sketch, "E13.24.4", {"start": v(36.66, 9.82) * mm, "end": v(35.1, 9.4) * mm});
            skArc(sketch, "E13.24.5", {"start": v(35.1, 9.4) * mm, "mid": v(34.63, 9.04) * mm, "end": v(34.54, 8.45) * mm});
            skArc(sketch, "E13.24.6", {"start": v(35.73, 13.65) * mm, "mid": v(35.58, 13.64) * mm, "end": v(35.43, 13.6) * mm});
            skArc(sketch, "E13.24.7", {"start": v(36.66, 9.82) * mm, "mid": v(36.8, 9.88) * mm, "end": v(36.93, 9.95) * mm});
            skLineSegment(sketch, "E13.24.8", {"start": v(38.78, 12.15) * mm, "end": v(38.66, 12.56) * mm});
            skArc(sketch, "E13.24.9", {"start": v(38.7, 11.69) * mm, "mid": v(38.8, 11.9) * mm, "end": v(38.78, 12.15) * mm});
            skLineSegment(sketch, "E13.24.10", {"start": v(38.57, 12.82) * mm, "end": v(38.66, 12.56) * mm});
            skArc(sketch, "E13.24.11", {"start": v(38.57, 12.82) * mm, "mid": v(38.36, 13.15) * mm, "end": v(38.02, 13.33) * mm});
            skLineSegment(sketch, "E13.25.0", {"start": v(31.83, 20.67) * mm, "end": v(30.48, 19.8) * mm});
            skArc(sketch, "E13.25.1", {"start": v(29.4, 20.01) * mm, "mid": v(29.9, 19.68) * mm, "end": v(30.48, 19.8) * mm});
            skArc(sketch, "E13.25.2", {"start": v(32.1, 20.78) * mm, "mid": v(33.26, 20.93) * mm, "end": v(34.42, 20.95) * mm});
            skArc(sketch, "E13.25.3", {"start": v(34.05, 17.41) * mm, "mid": v(34.8, 18.4) * mm, "end": v(35.42, 19.48) * mm});
            skLineSegment(sketch, "E13.25.4", {"start": v(33.81, 17.23) * mm, "end": v(32.38, 16.5) * mm});
            skArc(sketch, "E13.25.5", {"start": v(32.38, 16.5) * mm, "mid": v(32, 16.05) * mm, "end": v(32.03, 15.45) * mm});
            skArc(sketch, "E13.25.6", {"start": v(32.1, 20.78) * mm, "mid": v(31.96, 20.74) * mm, "end": v(31.83, 20.67) * mm});
            skArc(sketch, "E13.25.7", {"start": v(33.81, 17.23) * mm, "mid": v(33.94, 17.31) * mm, "end": v(34.05, 17.41) * mm});
            skLineSegment(sketch, "E13.25.8", {"start": v(35.4, 19.95) * mm, "end": v(35.2, 20.32) * mm});
            skArc(sketch, "E13.25.9", {"start": v(35.42, 19.48) * mm, "mid": v(35.47, 19.72) * mm, "end": v(35.4, 19.95) * mm});
            skLineSegment(sketch, "E13.25.10", {"start": v(35.06, 20.56) * mm, "end": v(35.2, 20.32) * mm});
            skArc(sketch, "E13.25.11", {"start": v(35.06, 20.56) * mm, "mid": v(34.79, 20.83) * mm, "end": v(34.42, 20.95) * mm});
            skLineSegment(sketch, "E13.26.0", {"start": v(26.83, 26.83) * mm, "end": v(25.7, 25.7) * mm});
            skArc(sketch, "E13.26.1", {"start": v(24.59, 25.69) * mm, "mid": v(25.15, 25.47) * mm, "end": v(25.7, 25.7) * mm});
            skArc(sketch, "E13.26.2", {"start": v(27.09, 27) * mm, "mid": v(28.18, 27.4) * mm, "end": v(29.31, 27.64) * mm});
            skArc(sketch, "E13.26.3", {"start": v(29.69, 24.11) * mm, "mid": v(30.22, 25.24) * mm, "end": v(30.6, 26.42) * mm});
            skLineSegment(sketch, "E13.26.4", {"start": v(29.5, 23.88) * mm, "end": v(28.25, 22.87) * mm});
            skArc(sketch, "E13.26.5", {"start": v(28.25, 22.87) * mm, "mid": v(27.96, 22.35) * mm, "end": v(28.12, 21.77) * mm});
            skArc(sketch, "E13.26.6", {"start": v(27.09, 27) * mm, "mid": v(26.95, 26.93) * mm, "end": v(26.83, 26.83) * mm});
            skArc(sketch, "E13.26.7", {"start": v(29.5, 23.88) * mm, "mid": v(29.6, 23.99) * mm, "end": v(29.69, 24.11) * mm});
            skLineSegment(sketch, "E13.26.8", {"start": v(30.49, 26.87) * mm, "end": v(30.2, 27.2) * mm});
            skArc(sketch, "E13.26.9", {"start": v(30.6, 26.42) * mm, "mid": v(30.6, 26.66) * mm, "end": v(30.49, 26.87) * mm});
            skLineSegment(sketch, "E13.26.10", {"start": v(30.02, 27.4) * mm, "end": v(30.2, 27.2) * mm});
            skArc(sketch, "E13.26.11", {"start": v(30.02, 27.4) * mm, "mid": v(29.7, 27.6) * mm, "end": v(29.31, 27.64) * mm});
            skLineSegment(sketch, "E13.27.0", {"start": v(20.67, 31.83) * mm, "end": v(19.8, 30.48) * mm});
            skArc(sketch, "E13.27.1", {"start": v(18.71, 30.24) * mm, "mid": v(19.3, 30.14) * mm, "end": v(19.8, 30.48) * mm});
            skArc(sketch, "E13.27.2", {"start": v(20.88, 32.04) * mm, "mid": v(21.87, 32.65) * mm, "end": v(22.92, 33.13) * mm});
            skArc(sketch, "E13.27.3", {"start": v(24.02, 29.76) * mm, "mid": v(24.3, 30.97) * mm, "end": v(24.44, 32.2) * mm});
            skLineSegment(sketch, "E13.27.4", {"start": v(23.88, 29.5) * mm, "end": v(22.87, 28.25) * mm});
            skArc(sketch, "E13.27.5", {"start": v(22.87, 28.25) * mm, "mid": v(22.7, 27.67) * mm, "end": v(22.98, 27.14) * mm});
            skArc(sketch, "E13.27.6", {"start": v(20.88, 32.04) * mm, "mid": v(20.76, 31.95) * mm, "end": v(20.67, 31.83) * mm});
            skArc(sketch, "E13.27.7", {"start": v(23.88, 29.5) * mm, "mid": v(23.97, 29.62) * mm, "end": v(24.02, 29.76) * mm});
            skLineSegment(sketch, "E13.27.8", {"start": v(24.23, 32.63) * mm, "end": v(23.9, 32.88) * mm});
            skArc(sketch, "E13.27.9", {"start": v(24.44, 32.2) * mm, "mid": v(24.39, 32.44) * mm, "end": v(24.23, 32.63) * mm});
            skLineSegment(sketch, "E13.27.10", {"start": v(23.66, 33.04) * mm, "end": v(23.9, 32.88) * mm});
            skArc(sketch, "E13.27.11", {"start": v(23.66, 33.04) * mm, "mid": v(23.3, 33.18) * mm, "end": v(22.92, 33.13) * mm});
            skLineSegment(sketch, "E13.28.0", {"start": v(13.6, 35.43) * mm, "end": v(13.02, 33.93) * mm});
            skArc(sketch, "E13.28.1", {"start": v(12.02, 33.47) * mm, "mid": v(12.61, 33.5) * mm, "end": v(13.02, 33.93) * mm});
            skArc(sketch, "E13.28.2", {"start": v(13.76, 35.69) * mm, "mid": v(14.6, 36.48) * mm, "end": v(15.53, 37.18) * mm});
            skArc(sketch, "E13.28.3", {"start": v(17.31, 34.1) * mm, "mid": v(17.34, 35.34) * mm, "end": v(17.2, 36.58) * mm});
            skLineSegment(sketch, "E13.28.4", {"start": v(17.23, 33.81) * mm, "end": v(16.5, 32.38) * mm});
            skArc(sketch, "E13.28.5", {"start": v(16.5, 32.38) * mm, "mid": v(16.45, 31.79) * mm, "end": v(16.83, 31.32) * mm});
            skArc(sketch, "E13.28.6", {"start": v(13.76, 35.69) * mm, "mid": v(13.67, 35.56) * mm, "end": v(13.6, 35.43) * mm});
            skArc(sketch, "E13.28.7", {"start": v(17.23, 33.81) * mm, "mid": v(17.28, 33.95) * mm, "end": v(17.31, 34.1) * mm});
            skLineSegment(sketch, "E13.28.8", {"start": v(16.92, 36.95) * mm, "end": v(16.53, 37.13) * mm});
            skArc(sketch, "E13.28.9", {"start": v(17.2, 36.58) * mm, "mid": v(17.1, 36.8) * mm, "end": v(16.92, 36.95) * mm});
            skLineSegment(sketch, "E13.28.10", {"start": v(16.28, 37.24) * mm, "end": v(16.53, 37.13) * mm});
            skArc(sketch, "E13.28.11", {"start": v(16.28, 37.24) * mm, "mid": v(15.9, 37.3) * mm, "end": v(15.53, 37.18) * mm});
            skLineSegment(sketch, "E13.29.0", {"start": v(5.94, 37.48) * mm, "end": v(5.69, 35.9) * mm});
            skArc(sketch, "E13.29.1", {"start": v(4.8, 35.24) * mm, "mid": v(5.38, 35.38) * mm, "end": v(5.69, 35.9) * mm});
            skArc(sketch, "E13.29.2", {"start": v(6.04, 37.77) * mm, "mid": v(6.7, 38.72) * mm, "end": v(7.46, 39.6) * mm});
            skArc(sketch, "E13.29.3", {"start": v(9.84, 36.96) * mm, "mid": v(9.61, 38.18) * mm, "end": v(9.23, 39.36) * mm});
            skLineSegment(sketch, "E13.29.4", {"start": v(9.82, 36.66) * mm, "end": v(9.4, 35.1) * mm});
            skArc(sketch, "E13.29.5", {"start": v(9.4, 35.1) * mm, "mid": v(9.48, 34.51) * mm, "end": v(9.95, 34.14) * mm});
            skArc(sketch, "E13.29.6", {"start": v(6.04, 37.77) * mm, "mid": v(5.97, 37.63) * mm, "end": v(5.94, 37.48) * mm});
            skArc(sketch, "E13.29.7", {"start": v(9.82, 36.66) * mm, "mid": v(9.85, 36.8) * mm, "end": v(9.84, 36.96) * mm});
            skLineSegment(sketch, "E13.29.8", {"start": v(8.87, 39.66) * mm, "end": v(8.45, 39.76) * mm});
            skArc(sketch, "E13.29.9", {"start": v(9.23, 39.36) * mm, "mid": v(9.08, 39.55) * mm, "end": v(8.87, 39.66) * mm});
            skLineSegment(sketch, "E13.29.10", {"start": v(8.18, 39.81) * mm, "end": v(8.45, 39.76) * mm});
            skArc(sketch, "E13.29.11", {"start": v(8.18, 39.81) * mm, "mid": v(7.8, 39.8) * mm, "end": v(7.46, 39.6) * mm});
            skArc(sketch, "E14.trimOffspring", {"start": v(-9.95, 34.14) * mm, "mid": v(-10.99, 33.82) * mm, "end": v(-12.02, 33.47) * mm});
            skArc(sketch, "E15.trimOffspring", {"start": v(-16.83, 31.32) * mm, "mid": v(-17.78, 30.8) * mm, "end": v(-18.71, 30.24) * mm});
            skArc(sketch, "E16.trimOffspring", {"start": v(-22.98, 27.14) * mm, "mid": v(-23.8, 26.43) * mm, "end": v(-24.59, 25.69) * mm});
            skArc(sketch, "E17.trimOffspring", {"start": v(4.8, 35.24) * mm, "mid": v(3.72, 35.37) * mm, "end": v(2.64, 35.46) * mm});
            skArc(sketch, "E18.trimOffspring", {"start": v(12.02, 33.47) * mm, "mid": v(10.99, 33.82) * mm, "end": v(9.95, 34.14) * mm});
            skArc(sketch, "E19.trimOffspring", {"start": v(18.71, 30.24) * mm, "mid": v(17.78, 30.8) * mm, "end": v(16.83, 31.32) * mm});
            skArc(sketch, "E20.trimOffspring", {"start": v(-28.12, 21.77) * mm, "mid": v(-28.77, 20.9) * mm, "end": v(-29.4, 20.01) * mm});
            skArc(sketch, "E21.trimOffspring", {"start": v(-32.03, 15.45) * mm, "mid": v(-32.49, 14.46) * mm, "end": v(-32.91, 13.47) * mm});
            skArc(sketch, "E22.trimOffspring", {"start": v(24.59, 25.69) * mm, "mid": v(23.8, 26.43) * mm, "end": v(22.98, 27.14) * mm});
            skArc(sketch, "E23.trimOffspring", {"start": v(29.4, 20.01) * mm, "mid": v(28.77, 20.9) * mm, "end": v(28.12, 21.77) * mm});
            skArc(sketch, "E24.trimOffspring", {"start": v(35, 6.33) * mm, "mid": v(34.78, 7.4) * mm, "end": v(34.54, 8.45) * mm});
            skArc(sketch, "E25.trimOffspring", {"start": v(35.54, -1.09) * mm, "mid": v(35.56, 0) * mm, "end": v(35.54, 1.09) * mm});
            skArc(sketch, "E26.trimOffspring", {"start": v(-35.54, 1.09) * mm, "mid": v(-35.56, 0) * mm, "end": v(-35.54, -1.09) * mm});
            skArc(sketch, "E27.trimOffspring", {"start": v(-35, -6.33) * mm, "mid": v(-34.78, -7.4) * mm, "end": v(-34.54, -8.45) * mm});
            skArc(sketch, "E28.trimOffspring", {"start": v(-32.91, -13.47) * mm, "mid": v(-32.49, -14.46) * mm, "end": v(-32.03, -15.45) * mm});
            skArc(sketch, "E29.trimOffspring", {"start": v(-29.4, -20.01) * mm, "mid": v(-28.77, -20.9) * mm, "end": v(-28.12, -21.77) * mm});
            skArc(sketch, "E30.trimOffspring", {"start": v(-24.59, -25.69) * mm, "mid": v(-23.8, -26.43) * mm, "end": v(-22.98, -27.14) * mm});
            skArc(sketch, "E31.trimOffspring", {"start": v(-18.71, -30.24) * mm, "mid": v(-17.78, -30.8) * mm, "end": v(-16.83, -31.32) * mm});
            skArc(sketch, "E32.trimOffspring", {"start": v(-12.02, -33.47) * mm, "mid": v(-10.99, -33.82) * mm, "end": v(-9.95, -34.14) * mm});
            skArc(sketch, "E33.trimOffspring", {"start": v(-4.8, -35.24) * mm, "mid": v(-3.72, -35.37) * mm, "end": v(-2.64, -35.46) * mm});
            skArc(sketch, "E34.trimOffspring", {"start": v(9.95, -34.14) * mm, "mid": v(10.99, -33.82) * mm, "end": v(12.02, -33.47) * mm});
            skArc(sketch, "E35.trimOffspring", {"start": v(2.64, -35.46) * mm, "mid": v(3.72, -35.37) * mm, "end": v(4.8, -35.24) * mm});
            skArc(sketch, "E36.trimOffspring", {"start": v(16.83, -31.32) * mm, "mid": v(17.78, -30.8) * mm, "end": v(18.71, -30.24) * mm});
            skArc(sketch, "E37.trimOffspring", {"start": v(22.98, -27.14) * mm, "mid": v(23.8, -26.43) * mm, "end": v(24.59, -25.69) * mm});
            skArc(sketch, "E38.trimOffspring", {"start": v(28.12, -21.77) * mm, "mid": v(28.77, -20.9) * mm, "end": v(29.4, -20.01) * mm});
            skArc(sketch, "E39.trimOffspring", {"start": v(32.03, -15.45) * mm, "mid": v(32.49, -14.46) * mm, "end": v(32.91, -13.47) * mm});
            skArc(sketch, "E40.trimOffspring", {"start": v(34.54, -8.45) * mm, "mid": v(34.78, -7.4) * mm, "end": v(35, -6.33) * mm});
            skLineSegment(sketch, "E41", {"start": v(32.91, 13.47) * mm, "end": v(32.03, 15.45) * mm});
            skLineSegment(sketch, "E42", {"start": v(-35, 6.33) * mm, "end": v(-34.54, 8.45) * mm});
            skSolve(sketch);
        }
        {
            var Q0;
            Q0=makeQuery(id+"F0.imprint","IMPRINT",FACE,{"disambiguationData":[TD([[makeQuery(id+"F0.imprint","IMPRINT",EDGE,{"derivedFrom":sQuery(id+"F0.wireOp",EDGE,"E0")}),1.0]])]});
            extrude(context, id + "F1", {"entities" : qUnion([Q0]), "depth" : 114.3 * mm});
        }
        {
            var Q0;
            Q0=makeQuery(id+"F1.opExtrude","CAP_FACE",FACE,{"disambiguationData":[OSD([sQuery(id+"F0.wireOp",EDGE,"E0"),sQuery(id+"F0.wireOp",EDGE,"E1.trimOffspring"),sQuery(id+"F0.wireOp",EDGE,"E2"),sQuery(id+"F0.wireOp",EDGE,"E3"),sQuery(id+"F0.wireOp",EDGE,"E4.MirrorCS"),sQuery(id+"F0.wireOp",EDGE,"E5.MirrorCS"),sQuery(id+"F0.wireOp",EDGE,"E6.MirrorCS"),sQuery(id+"F0.wireOp",EDGE,"E7.filletArc"),sQuery(id+"F0.wireOp",EDGE,"E8.filletArc"),sQuery(id+"F0.wireOp",EDGE,"E9.filletArc"),sQuery(id+"F0.wireOp",EDGE,"E10.filletArc"),sQuery(id+"F0.wireOp",EDGE,"E11.filletArc"),sQuery(id+"F0.wireOp",EDGE,"E12.filletArc"),sQuery(id+"F0.wireOp",EDGE,"E13.1.0"),sQuery(id+"F0.wireOp",EDGE,"E13.1.1"),sQuery(id+"F0.wireOp",EDGE,"E13.1.2"),sQuery(id+"F0.wireOp",EDGE,"E13.1.3"),sQuery(id+"F0.wireOp",EDGE,"E13.1.4"),sQuery(id+"F0.wireOp",EDGE,"E13.1.5"),sQuery(id+"F0.wireOp",EDGE,"E13.1.6"),sQuery(id+"F0.wireOp",EDGE,"E13.1.7"),sQuery(id+"F0.wireOp",EDGE,"E13.1.8"),sQuery(id+"F0.wireOp",EDGE,"E13.1.9"),sQuery(id+"F0.wireOp",EDGE,"E13.1.10"),sQuery(id+"F0.wireOp",EDGE,"E13.1.11"),sQuery(id+"F0.wireOp",EDGE,"E13.2.0"),sQuery(id+"F0.wireOp",EDGE,"E13.2.1"),sQuery(id+"F0.wireOp",EDGE,"E13.2.2"),sQuery(id+"F0.wireOp",EDGE,"E13.2.3"),sQuery(id+"F0.wireOp",EDGE,"E13.2.4"),sQuery(id+"F0.wireOp",EDGE,"E13.2.5"),sQuery(id+"F0.wireOp",EDGE,"E13.2.6"),sQuery(id+"F0.wireOp",EDGE,"E13.2.7"),sQuery(id+"F0.wireOp",EDGE,"E13.2.8"),sQuery(id+"F0.wireOp",EDGE,"E13.2.9"),sQuery(id+"F0.wireOp",EDGE,"E13.2.10"),sQuery(id+"F0.wireOp",EDGE,"E13.2.11"),sQuery(id+"F0.wireOp",EDGE,"E13.3.0"),sQuery(id+"F0.wireOp",EDGE,"E13.3.1"),sQuery(id+"F0.wireOp",EDGE,"E13.3.2"),sQuery(id+"F0.wireOp",EDGE,"E13.3.3"),sQuery(id+"F0.wireOp",EDGE,"E13.3.4"),sQuery(id+"F0.wireOp",EDGE,"E13.3.5"),sQuery(id+"F0.wireOp",EDGE,"E13.3.6"),sQuery(id+"F0.wireOp",EDGE,"E13.3.7"),sQuery(id+"F0.wireOp",EDGE,"E13.3.8"),sQuery(id+"F0.wireOp",EDGE,"E13.3.9"),sQuery(id+"F0.wireOp",EDGE,"E13.3.10"),sQuery(id+"F0.wireOp",EDGE,"E13.3.11"),sQuery(id+"F0.wireOp",EDGE,"E13.4.0"),sQuery(id+"F0.wireOp",EDGE,"E13.4.1"),sQuery(id+"F0.wireOp",EDGE,"E13.4.2"),sQuery(id+"F0.wireOp",EDGE,"E13.4.3"),sQuery(id+"F0.wireOp",EDGE,"E13.4.4"),sQuery(id+"F0.wireOp",EDGE,"E13.4.5"),sQuery(id+"F0.wireOp",EDGE,"E13.4.6"),sQuery(id+"F0.wireOp",EDGE,"E13.4.7"),sQuery(id+"F0.wireOp",EDGE,"E13.4.8"),sQuery(id+"F0.wireOp",EDGE,"E13.4.9"),sQuery(id+"F0.wireOp",EDGE,"E13.4.10"),sQuery(id+"F0.wireOp",EDGE,"E13.4.11"),sQuery(id+"F0.wireOp",EDGE,"E13.5.0"),sQuery(id+"F0.wireOp",EDGE,"E13.5.1"),sQuery(id+"F0.wireOp",EDGE,"E13.5.2"),sQuery(id+"F0.wireOp",EDGE,"E13.5.3"),sQuery(id+"F0.wireOp",EDGE,"E13.5.4"),sQuery(id+"F0.wireOp",EDGE,"E13.5.5"),sQuery(id+"F0.wireOp",EDGE,"E13.5.6"),sQuery(id+"F0.wireOp",EDGE,"E13.5.7"),sQuery(id+"F0.wireOp",EDGE,"E13.5.8"),sQuery(id+"F0.wireOp",EDGE,"E13.5.9"),sQuery(id+"F0.wireOp",EDGE,"E13.5.10"),sQuery(id+"F0.wireOp",EDGE,"E13.5.11"),sQuery(id+"F0.wireOp",EDGE,"E13.6.0"),sQuery(id+"F0.wireOp",EDGE,"E13.6.1"),sQuery(id+"F0.wireOp",EDGE,"E13.6.2"),sQuery(id+"F0.wireOp",EDGE,"E13.6.3"),sQuery(id+"F0.wireOp",EDGE,"E13.6.4"),sQuery(id+"F0.wireOp",EDGE,"E13.6.5"),sQuery(id+"F0.wireOp",EDGE,"E13.6.6"),sQuery(id+"F0.wireOp",EDGE,"E13.6.7"),sQuery(id+"F0.wireOp",EDGE,"E13.6.8"),sQuery(id+"F0.wireOp",EDGE,"E13.6.9"),sQuery(id+"F0.wireOp",EDGE,"E13.6.10"),sQuery(id+"F0.wireOp",EDGE,"E13.6.11"),sQuery(id+"F0.wireOp",EDGE,"E13.7.0"),sQuery(id+"F0.wireOp",EDGE,"E13.7.1"),sQuery(id+"F0.wireOp",EDGE,"E13.7.2"),sQuery(id+"F0.wireOp",EDGE,"E13.7.3"),sQuery(id+"F0.wireOp",EDGE,"E13.7.4"),sQuery(id+"F0.wireOp",EDGE,"E13.7.5"),sQuery(id+"F0.wireOp",EDGE,"E13.7.6"),sQuery(id+"F0.wireOp",EDGE,"E13.7.7"),sQuery(id+"F0.wireOp",EDGE,"E13.7.8"),sQuery(id+"F0.wireOp",EDGE,"E13.7.9"),sQuery(id+"F0.wireOp",EDGE,"E13.7.10"),sQuery(id+"F0.wireOp",EDGE,"E13.7.11"),sQuery(id+"F0.wireOp",EDGE,"E13.8.0"),sQuery(id+"F0.wireOp",EDGE,"E13.8.1"),sQuery(id+"F0.wireOp",EDGE,"E13.8.2"),sQuery(id+"F0.wireOp",EDGE,"E13.8.3"),sQuery(id+"F0.wireOp",EDGE,"E13.8.4"),sQuery(id+"F0.wireOp",EDGE,"E13.8.5"),sQuery(id+"F0.wireOp",EDGE,"E13.8.6"),sQuery(id+"F0.wireOp",EDGE,"E13.8.7"),sQuery(id+"F0.wireOp",EDGE,"E13.8.8"),sQuery(id+"F0.wireOp",EDGE,"E13.8.9"),sQuery(id+"F0.wireOp",EDGE,"E13.8.10"),sQuery(id+"F0.wireOp",EDGE,"E13.8.11"),sQuery(id+"F0.wireOp",EDGE,"E13.9.0"),sQuery(id+"F0.wireOp",EDGE,"E13.9.1"),sQuery(id+"F0.wireOp",EDGE,"E13.9.2"),sQuery(id+"F0.wireOp",EDGE,"E13.9.3"),sQuery(id+"F0.wireOp",EDGE,"E13.9.4"),sQuery(id+"F0.wireOp",EDGE,"E13.9.5"),sQuery(id+"F0.wireOp",EDGE,"E13.9.6"),sQuery(id+"F0.wireOp",EDGE,"E13.9.7"),sQuery(id+"F0.wireOp",EDGE,"E13.9.8"),sQuery(id+"F0.wireOp",EDGE,"E13.9.9"),sQuery(id+"F0.wireOp",EDGE,"E13.9.10"),sQuery(id+"F0.wireOp",EDGE,"E13.9.11"),sQuery(id+"F0.wireOp",EDGE,"E13.10.0"),sQuery(id+"F0.wireOp",EDGE,"E13.10.1"),sQuery(id+"F0.wireOp",EDGE,"E13.10.2"),sQuery(id+"F0.wireOp",EDGE,"E13.10.3"),sQuery(id+"F0.wireOp",EDGE,"E13.10.4"),sQuery(id+"F0.wireOp",EDGE,"E13.10.5"),sQuery(id+"F0.wireOp",EDGE,"E13.10.6"),sQuery(id+"F0.wireOp",EDGE,"E13.10.7"),sQuery(id+"F0.wireOp",EDGE,"E13.10.8"),sQuery(id+"F0.wireOp",EDGE,"E13.10.9"),sQuery(id+"F0.wireOp",EDGE,"E13.10.10"),sQuery(id+"F0.wireOp",EDGE,"E13.10.11"),sQuery(id+"F0.wireOp",EDGE,"E13.11.0"),sQuery(id+"F0.wireOp",EDGE,"E13.11.1"),sQuery(id+"F0.wireOp",EDGE,"E13.11.2"),sQuery(id+"F0.wireOp",EDGE,"E13.11.3"),sQuery(id+"F0.wireOp",EDGE,"E13.11.4"),sQuery(id+"F0.wireOp",EDGE,"E13.11.5"),sQuery(id+"F0.wireOp",EDGE,"E13.11.6"),sQuery(id+"F0.wireOp",EDGE,"E13.11.7"),sQuery(id+"F0.wireOp",EDGE,"E13.11.8"),sQuery(id+"F0.wireOp",EDGE,"E13.11.9"),sQuery(id+"F0.wireOp",EDGE,"E13.11.10"),sQuery(id+"F0.wireOp",EDGE,"E13.11.11"),sQuery(id+"F0.wireOp",EDGE,"E13.12.0"),sQuery(id+"F0.wireOp",EDGE,"E13.12.1"),sQuery(id+"F0.wireOp",EDGE,"E13.12.2"),sQuery(id+"F0.wireOp",EDGE,"E13.12.3"),sQuery(id+"F0.wireOp",EDGE,"E13.12.4"),sQuery(id+"F0.wireOp",EDGE,"E13.12.5"),sQuery(id+"F0.wireOp",EDGE,"E13.12.6"),sQuery(id+"F0.wireOp",EDGE,"E13.12.7"),sQuery(id+"F0.wireOp",EDGE,"E13.12.8"),sQuery(id+"F0.wireOp",EDGE,"E13.12.9"),sQuery(id+"F0.wireOp",EDGE,"E13.12.10"),sQuery(id+"F0.wireOp",EDGE,"E13.12.11"),sQuery(id+"F0.wireOp",EDGE,"E13.13.0"),sQuery(id+"F0.wireOp",EDGE,"E13.13.1"),sQuery(id+"F0.wireOp",EDGE,"E13.13.2"),sQuery(id+"F0.wireOp",EDGE,"E13.13.3"),sQuery(id+"F0.wireOp",EDGE,"E13.13.4"),sQuery(id+"F0.wireOp",EDGE,"E13.13.5"),sQuery(id+"F0.wireOp",EDGE,"E13.13.6"),sQuery(id+"F0.wireOp",EDGE,"E13.13.7"),sQuery(id+"F0.wireOp",EDGE,"E13.13.8"),sQuery(id+"F0.wireOp",EDGE,"E13.13.9"),sQuery(id+"F0.wireOp",EDGE,"E13.13.10"),sQuery(id+"F0.wireOp",EDGE,"E13.13.11"),sQuery(id+"F0.wireOp",EDGE,"E13.14.0"),sQuery(id+"F0.wireOp",EDGE,"E13.14.1"),sQuery(id+"F0.wireOp",EDGE,"E13.14.2"),sQuery(id+"F0.wireOp",EDGE,"E13.14.3"),sQuery(id+"F0.wireOp",EDGE,"E13.14.4"),sQuery(id+"F0.wireOp",EDGE,"E13.14.5"),sQuery(id+"F0.wireOp",EDGE,"E13.14.6"),sQuery(id+"F0.wireOp",EDGE,"E13.14.7"),sQuery(id+"F0.wireOp",EDGE,"E13.14.8"),sQuery(id+"F0.wireOp",EDGE,"E13.14.9"),sQuery(id+"F0.wireOp",EDGE,"E13.14.10"),sQuery(id+"F0.wireOp",EDGE,"E13.14.11"),sQuery(id+"F0.wireOp",EDGE,"E13.15.0"),sQuery(id+"F0.wireOp",EDGE,"E13.15.1"),sQuery(id+"F0.wireOp",EDGE,"E13.15.2"),sQuery(id+"F0.wireOp",EDGE,"E13.15.3"),sQuery(id+"F0.wireOp",EDGE,"E13.15.4"),sQuery(id+"F0.wireOp",EDGE,"E13.15.5"),sQuery(id+"F0.wireOp",EDGE,"E13.15.6"),sQuery(id+"F0.wireOp",EDGE,"E13.15.7"),sQuery(id+"F0.wireOp",EDGE,"E13.15.8"),sQuery(id+"F0.wireOp",EDGE,"E13.15.9"),sQuery(id+"F0.wireOp",EDGE,"E13.15.10"),sQuery(id+"F0.wireOp",EDGE,"E13.15.11"),sQuery(id+"F0.wireOp",EDGE,"E13.16.0"),sQuery(id+"F0.wireOp",EDGE,"E13.16.1"),sQuery(id+"F0.wireOp",EDGE,"E13.16.2"),sQuery(id+"F0.wireOp",EDGE,"E13.16.3"),sQuery(id+"F0.wireOp",EDGE,"E13.16.4"),sQuery(id+"F0.wireOp",EDGE,"E13.16.5"),sQuery(id+"F0.wireOp",EDGE,"E13.16.6"),sQuery(id+"F0.wireOp",EDGE,"E13.16.7"),sQuery(id+"F0.wireOp",EDGE,"E13.16.8"),sQuery(id+"F0.wireOp",EDGE,"E13.16.9"),sQuery(id+"F0.wireOp",EDGE,"E13.16.10"),sQuery(id+"F0.wireOp",EDGE,"E13.16.11"),sQuery(id+"F0.wireOp",EDGE,"E13.17.0"),sQuery(id+"F0.wireOp",EDGE,"E13.17.1"),sQuery(id+"F0.wireOp",EDGE,"E13.17.2"),sQuery(id+"F0.wireOp",EDGE,"E13.17.3"),sQuery(id+"F0.wireOp",EDGE,"E13.17.4"),sQuery(id+"F0.wireOp",EDGE,"E13.17.5"),sQuery(id+"F0.wireOp",EDGE,"E13.17.6"),sQuery(id+"F0.wireOp",EDGE,"E13.17.7"),sQuery(id+"F0.wireOp",EDGE,"E13.17.8"),sQuery(id+"F0.wireOp",EDGE,"E13.17.9"),sQuery(id+"F0.wireOp",EDGE,"E13.17.10"),sQuery(id+"F0.wireOp",EDGE,"E13.17.11"),sQuery(id+"F0.wireOp",EDGE,"E13.18.0"),sQuery(id+"F0.wireOp",EDGE,"E13.18.1"),sQuery(id+"F0.wireOp",EDGE,"E13.18.2"),sQuery(id+"F0.wireOp",EDGE,"E13.18.3"),sQuery(id+"F0.wireOp",EDGE,"E13.18.4"),sQuery(id+"F0.wireOp",EDGE,"E13.18.5"),sQuery(id+"F0.wireOp",EDGE,"E13.18.6"),sQuery(id+"F0.wireOp",EDGE,"E13.18.7"),sQuery(id+"F0.wireOp",EDGE,"E13.18.8"),sQuery(id+"F0.wireOp",EDGE,"E13.18.9"),sQuery(id+"F0.wireOp",EDGE,"E13.18.10"),sQuery(id+"F0.wireOp",EDGE,"E13.18.11"),sQuery(id+"F0.wireOp",EDGE,"E13.19.0"),sQuery(id+"F0.wireOp",EDGE,"E13.19.1"),sQuery(id+"F0.wireOp",EDGE,"E13.19.2"),sQuery(id+"F0.wireOp",EDGE,"E13.19.3"),sQuery(id+"F0.wireOp",EDGE,"E13.19.4"),sQuery(id+"F0.wireOp",EDGE,"E13.19.5"),sQuery(id+"F0.wireOp",EDGE,"E13.19.6"),sQuery(id+"F0.wireOp",EDGE,"E13.19.7"),sQuery(id+"F0.wireOp",EDGE,"E13.19.8"),sQuery(id+"F0.wireOp",EDGE,"E13.19.9"),sQuery(id+"F0.wireOp",EDGE,"E13.19.10"),sQuery(id+"F0.wireOp",EDGE,"E13.19.11"),sQuery(id+"F0.wireOp",EDGE,"E13.20.0"),sQuery(id+"F0.wireOp",EDGE,"E13.20.1"),sQuery(id+"F0.wireOp",EDGE,"E13.20.2"),sQuery(id+"F0.wireOp",EDGE,"E13.20.3"),sQuery(id+"F0.wireOp",EDGE,"E13.20.4"),sQuery(id+"F0.wireOp",EDGE,"E13.20.5"),sQuery(id+"F0.wireOp",EDGE,"E13.20.6"),sQuery(id+"F0.wireOp",EDGE,"E13.20.7"),sQuery(id+"F0.wireOp",EDGE,"E13.20.8"),sQuery(id+"F0.wireOp",EDGE,"E13.20.9"),sQuery(id+"F0.wireOp",EDGE,"E13.20.10"),sQuery(id+"F0.wireOp",EDGE,"E13.20.11"),sQuery(id+"F0.wireOp",EDGE,"E13.21.0"),sQuery(id+"F0.wireOp",EDGE,"E13.21.1"),sQuery(id+"F0.wireOp",EDGE,"E13.21.2"),sQuery(id+"F0.wireOp",EDGE,"E13.21.3"),sQuery(id+"F0.wireOp",EDGE,"E13.21.4"),sQuery(id+"F0.wireOp",EDGE,"E13.21.5"),sQuery(id+"F0.wireOp",EDGE,"E13.21.6"),sQuery(id+"F0.wireOp",EDGE,"E13.21.7"),sQuery(id+"F0.wireOp",EDGE,"E13.21.8"),sQuery(id+"F0.wireOp",EDGE,"E13.21.9"),sQuery(id+"F0.wireOp",EDGE,"E13.21.10"),sQuery(id+"F0.wireOp",EDGE,"E13.21.11"),sQuery(id+"F0.wireOp",EDGE,"E13.22.0"),sQuery(id+"F0.wireOp",EDGE,"E13.22.1"),sQuery(id+"F0.wireOp",EDGE,"E13.22.2"),sQuery(id+"F0.wireOp",EDGE,"E13.22.3"),sQuery(id+"F0.wireOp",EDGE,"E13.22.4"),sQuery(id+"F0.wireOp",EDGE,"E13.22.5"),sQuery(id+"F0.wireOp",EDGE,"E13.22.6"),sQuery(id+"F0.wireOp",EDGE,"E13.22.7"),sQuery(id+"F0.wireOp",EDGE,"E13.22.8"),sQuery(id+"F0.wireOp",EDGE,"E13.22.9"),sQuery(id+"F0.wireOp",EDGE,"E13.22.10"),sQuery(id+"F0.wireOp",EDGE,"E13.22.11"),sQuery(id+"F0.wireOp",EDGE,"E13.23.0"),sQuery(id+"F0.wireOp",EDGE,"E13.23.1"),sQuery(id+"F0.wireOp",EDGE,"E13.23.2"),sQuery(id+"F0.wireOp",EDGE,"E13.23.3"),sQuery(id+"F0.wireOp",EDGE,"E13.23.4"),sQuery(id+"F0.wireOp",EDGE,"E13.23.5"),sQuery(id+"F0.wireOp",EDGE,"E13.23.6"),sQuery(id+"F0.wireOp",EDGE,"E13.23.7"),sQuery(id+"F0.wireOp",EDGE,"E13.23.8"),sQuery(id+"F0.wireOp",EDGE,"E13.23.9"),sQuery(id+"F0.wireOp",EDGE,"E13.23.10"),sQuery(id+"F0.wireOp",EDGE,"E13.23.11"),sQuery(id+"F0.wireOp",EDGE,"E13.24.0"),sQuery(id+"F0.wireOp",EDGE,"E13.24.1"),sQuery(id+"F0.wireOp",EDGE,"E13.24.2"),sQuery(id+"F0.wireOp",EDGE,"E13.24.3"),sQuery(id+"F0.wireOp",EDGE,"E13.24.4"),sQuery(id+"F0.wireOp",EDGE,"E13.24.5"),sQuery(id+"F0.wireOp",EDGE,"E13.24.6"),sQuery(id+"F0.wireOp",EDGE,"E13.24.7"),sQuery(id+"F0.wireOp",EDGE,"E13.24.8"),sQuery(id+"F0.wireOp",EDGE,"E13.24.9"),sQuery(id+"F0.wireOp",EDGE,"E13.24.10"),sQuery(id+"F0.wireOp",EDGE,"E13.24.11"),sQuery(id+"F0.wireOp",EDGE,"E13.25.0"),sQuery(id+"F0.wireOp",EDGE,"E13.25.1"),sQuery(id+"F0.wireOp",EDGE,"E13.25.2"),sQuery(id+"F0.wireOp",EDGE,"E13.25.3"),sQuery(id+"F0.wireOp",EDGE,"E13.25.4"),sQuery(id+"F0.wireOp",EDGE,"E13.25.5"),sQuery(id+"F0.wireOp",EDGE,"E13.25.6"),sQuery(id+"F0.wireOp",EDGE,"E13.25.7"),sQuery(id+"F0.wireOp",EDGE,"E13.25.8"),sQuery(id+"F0.wireOp",EDGE,"E13.25.9"),sQuery(id+"F0.wireOp",EDGE,"E13.25.10"),sQuery(id+"F0.wireOp",EDGE,"E13.25.11"),sQuery(id+"F0.wireOp",EDGE,"E13.26.0"),sQuery(id+"F0.wireOp",EDGE,"E13.26.1"),sQuery(id+"F0.wireOp",EDGE,"E13.26.2"),sQuery(id+"F0.wireOp",EDGE,"E13.26.3"),sQuery(id+"F0.wireOp",EDGE,"E13.26.4"),sQuery(id+"F0.wireOp",EDGE,"E13.26.5"),sQuery(id+"F0.wireOp",EDGE,"E13.26.6"),sQuery(id+"F0.wireOp",EDGE,"E13.26.7"),sQuery(id+"F0.wireOp",EDGE,"E13.26.8"),sQuery(id+"F0.wireOp",EDGE,"E13.26.9"),sQuery(id+"F0.wireOp",EDGE,"E13.26.10"),sQuery(id+"F0.wireOp",EDGE,"E13.26.11"),sQuery(id+"F0.wireOp",EDGE,"E13.27.0"),sQuery(id+"F0.wireOp",EDGE,"E13.27.1"),sQuery(id+"F0.wireOp",EDGE,"E13.27.2"),sQuery(id+"F0.wireOp",EDGE,"E13.27.3"),sQuery(id+"F0.wireOp",EDGE,"E13.27.4"),sQuery(id+"F0.wireOp",EDGE,"E13.27.5"),sQuery(id+"F0.wireOp",EDGE,"E13.27.6"),sQuery(id+"F0.wireOp",EDGE,"E13.27.7"),sQuery(id+"F0.wireOp",EDGE,"E13.27.8"),sQuery(id+"F0.wireOp",EDGE,"E13.27.9"),sQuery(id+"F0.wireOp",EDGE,"E13.27.10"),sQuery(id+"F0.wireOp",EDGE,"E13.27.11"),sQuery(id+"F0.wireOp",EDGE,"E13.28.0"),sQuery(id+"F0.wireOp",EDGE,"E13.28.1"),sQuery(id+"F0.wireOp",EDGE,"E13.28.2"),sQuery(id+"F0.wireOp",EDGE,"E13.28.3"),sQuery(id+"F0.wireOp",EDGE,"E13.28.4"),sQuery(id+"F0.wireOp",EDGE,"E13.28.5"),sQuery(id+"F0.wireOp",EDGE,"E13.28.6"),sQuery(id+"F0.wireOp",EDGE,"E13.28.7"),sQuery(id+"F0.wireOp",EDGE,"E13.28.8"),sQuery(id+"F0.wireOp",EDGE,"E13.28.9"),sQuery(id+"F0.wireOp",EDGE,"E13.28.10"),sQuery(id+"F0.wireOp",EDGE,"E13.28.11"),sQuery(id+"F0.wireOp",EDGE,"E13.29.0"),sQuery(id+"F0.wireOp",EDGE,"E13.29.1"),sQuery(id+"F0.wireOp",EDGE,"E13.29.2"),sQuery(id+"F0.wireOp",EDGE,"E13.29.3"),sQuery(id+"F0.wireOp",EDGE,"E13.29.4"),sQuery(id+"F0.wireOp",EDGE,"E13.29.5"),sQuery(id+"F0.wireOp",EDGE,"E13.29.6"),sQuery(id+"F0.wireOp",EDGE,"E13.29.7"),sQuery(id+"F0.wireOp",EDGE,"E13.29.8"),sQuery(id+"F0.wireOp",EDGE,"E13.29.9"),sQuery(id+"F0.wireOp",EDGE,"E13.29.10"),sQuery(id+"F0.wireOp",EDGE,"E13.29.11"),sQuery(id+"F0.wireOp",EDGE,"E14.trimOffspring"),sQuery(id+"F0.wireOp",EDGE,"E15.trimOffspring"),sQuery(id+"F0.wireOp",EDGE,"E16.trimOffspring"),sQuery(id+"F0.wireOp",EDGE,"E17.trimOffspring"),sQuery(id+"F0.wireOp",EDGE,"E18.trimOffspring"),sQuery(id+"F0.wireOp",EDGE,"E19.trimOffspring"),sQuery(id+"F0.wireOp",EDGE,"E20.trimOffspring"),sQuery(id+"F0.wireOp",EDGE,"E21.trimOffspring"),sQuery(id+"F0.wireOp",EDGE,"E22.trimOffspring"),sQuery(id+"F0.wireOp",EDGE,"E23.trimOffspring"),sQuery(id+"F0.wireOp",EDGE,"E24.trimOffspring"),sQuery(id+"F0.wireOp",EDGE,"E25.trimOffspring"),sQuery(id+"F0.wireOp",EDGE,"E26.trimOffspring"),sQuery(id+"F0.wireOp",EDGE,"E27.trimOffspring"),sQuery(id+"F0.wireOp",EDGE,"E28.trimOffspring"),sQuery(id+"F0.wireOp",EDGE,"E29.trimOffspring"),sQuery(id+"F0.wireOp",EDGE,"E30.trimOffspring"),sQuery(id+"F0.wireOp",EDGE,"E31.trimOffspring"),sQuery(id+"F0.wireOp",EDGE,"E32.trimOffspring"),sQuery(id+"F0.wireOp",EDGE,"E33.trimOffspring"),sQuery(id+"F0.wireOp",EDGE,"E34.trimOffspring"),sQuery(id+"F0.wireOp",EDGE,"E35.trimOffspring"),sQuery(id+"F0.wireOp",EDGE,"E36.trimOffspring"),sQuery(id+"F0.wireOp",EDGE,"E37.trimOffspring"),sQuery(id+"F0.wireOp",EDGE,"E38.trimOffspring"),sQuery(id+"F0.wireOp",EDGE,"E39.trimOffspring"),sQuery(id+"F0.wireOp",EDGE,"E40.trimOffspring"),sQuery(id+"F0.wireOp",EDGE,"E41"),sQuery(id+"F0.wireOp",EDGE,"E42")])],"isStart":false});
            var sketch = newSketch(context, id + "F2", { "sketchPlane" : qUnion([Q0])});
            skCircle(sketch, "E43", {"center": v(0, 0) * mm, "radius": 12.7 * mm});
            skCircle(sketch, "E44", {"center": v(0, 0) * mm, "radius": 6.35 * mm});
            skSolve(sketch);
        }
        {
            var Q0;
            Q0=makeQuery(id+"F2.imprint","IMPRINT",FACE,{"disambiguationData":[TD([[makeQuery(id+"F2.imprint","IMPRINT",EDGE,{"derivedFrom":sQuery(id+"F2.wireOp",EDGE,"E44")}),1.0]])]});
            extrude(context, id + "F3", {"entities" : qUnion([Q0]), "operationType" : NewBodyOperationType.REMOVE, "oppositeDirection" : true, "depth" : 114.3 * mm});
        }
    });
